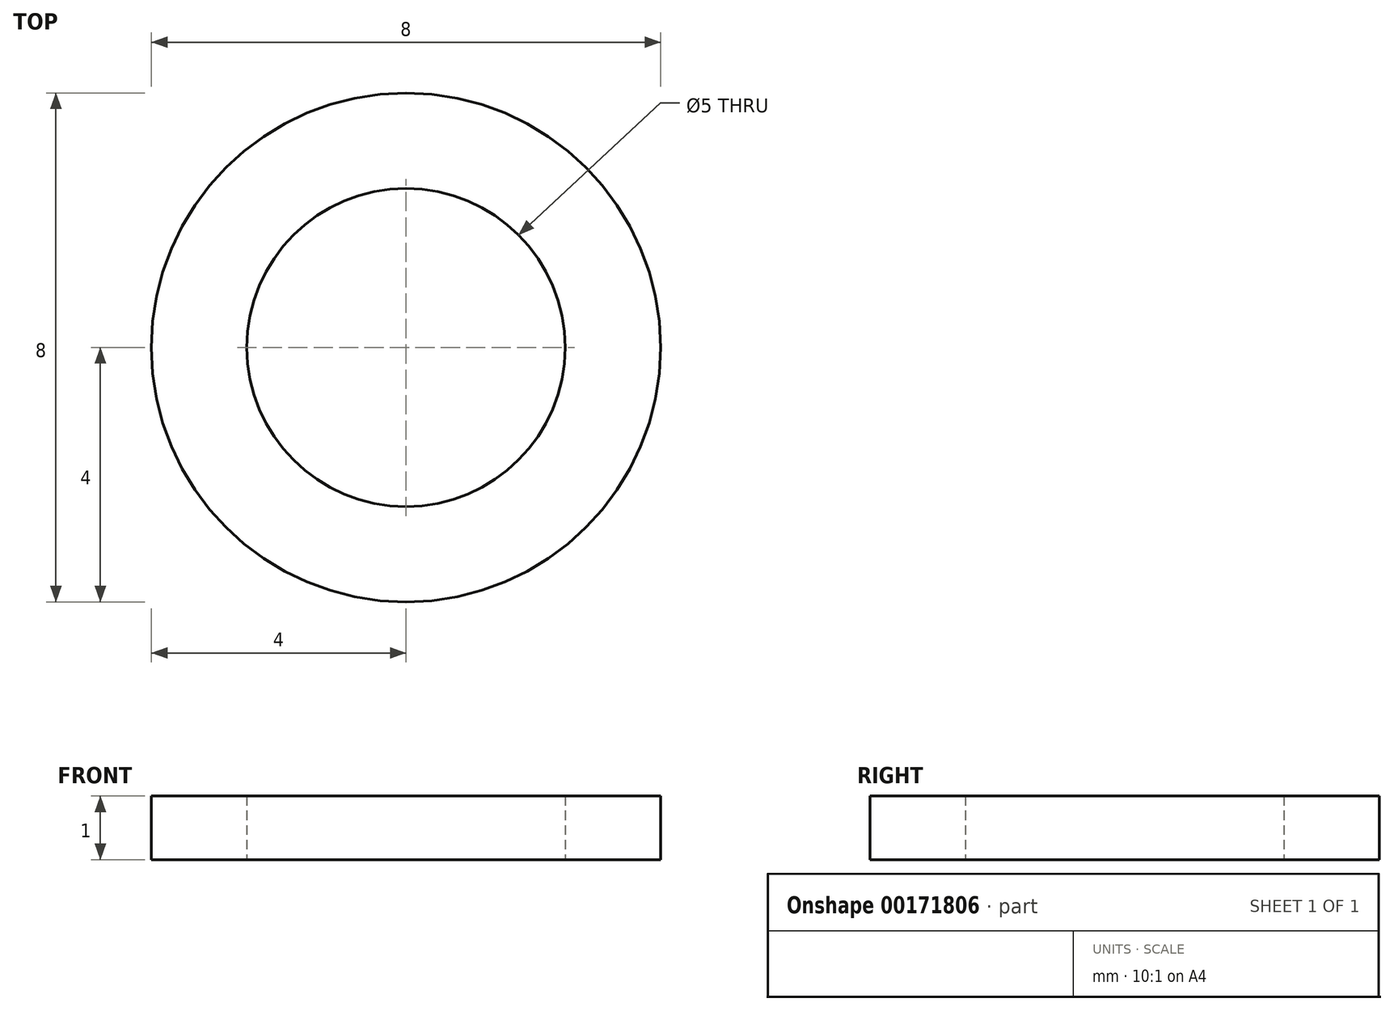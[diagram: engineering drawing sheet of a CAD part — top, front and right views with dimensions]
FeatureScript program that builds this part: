
annotation { "Feature Type Name" : "Feature", "Feature Type Description" : "" }
export const myFeature = defineFeature(function(context is Context, id is Id, definition is map)
    precondition{}
    {
        {
            var Q0;
            Q0=qCreatedBy(makeId("Top.planeOp"),FACE);
            var sketch = newSketch(context, id + "F0", { "sketchPlane" : qUnion([Q0])});
            skCircle(sketch, "E0", {"center": v(0, 0) * mm, "radius": 4 * mm});
            skCircle(sketch, "E1", {"center": v(0, 0) * mm, "radius": 2.5 * mm});
            skSolve(sketch);
        }
        {
            var Q0;
            Q0 = qSketchRegion(id + "F0", true);
            extrude(context, id + "F1", {"entities" : qUnion([Q0]), "depth" : 1 * mm});
        }
    });
